# Revit family: Toilet-Wall_Mount-KOHLER-VEIL-K-5402T.rfa_
name_source: partatom
category: Plumbing Fixtures
units: mm (PartAtom-declared; Revit-internal decimal feet)

## family parameters
Cut with Voids When Loaded = No
Host = Face
OmniClass Number = 23.31.19.17
OmniClass Title = Toilets With Tank
Part Type = Normal
Room Calculation Point = No
Round Connector Dimension = Use Diameter
Shared = No

## types (3) — shared parameters
ADA Compliant = No
Apparent Load = 2400 VA
Assembly Code = D2010100
CW Connection = Yes
Cold Water Inlet = Cold Water Inlet
Date Modified = 02/07/2024
Default Elevation = 0"
Electrical Connector = Yes
Electrical Note = One Dedicated Circuit Required
Finish = Kohler-Vitreous_China-0-White
Flow Rate = 0 GPM
Flush Rate- GPF = GPF
Flush Rate- LPF = 4.5 LPF
HW Connection = No
Hot Water Inlet = Hot Water Inlet
Length = 26 1/2"
Manufacturer = Kohler Co.
Master Format 2014 = 22 42 13.13
Master Format 2014 Name = Residential Water Closets
Material = Vitreous China
Pressure = 108.00 psi
Product Name = Veil
Seat Included = No
URL = http://www.kohler.com.cn
Vent Connection = No
Voltage = 240 V
Waste Connection = Yes
Waste Water Inlet = Waste Water Inlet
Waste Water Outlet = Waste Water Outlet
WaterSense Certified = No
Width = 18 13/16"

## per-type parameters (varying)
| type | Description | Model | Product Page URL | Type |
| 0-White | Intelligent Toilet Wall Hung | K-5402T-5-0 |  | 1 |
| 5, 0-White | Intelligent Toilet Wall Hung | K-5402T-5-0 | https://www.kohler.com.cn | 2 |
| 5XP, 0-White | Intelligent Toilet Wall Hung(IOT) | K-5402T-5XP-0 |  | 3 |

## geometry (parser evidence)
native form markers: Sweep x7
no freeform markers — native parametric forms only
